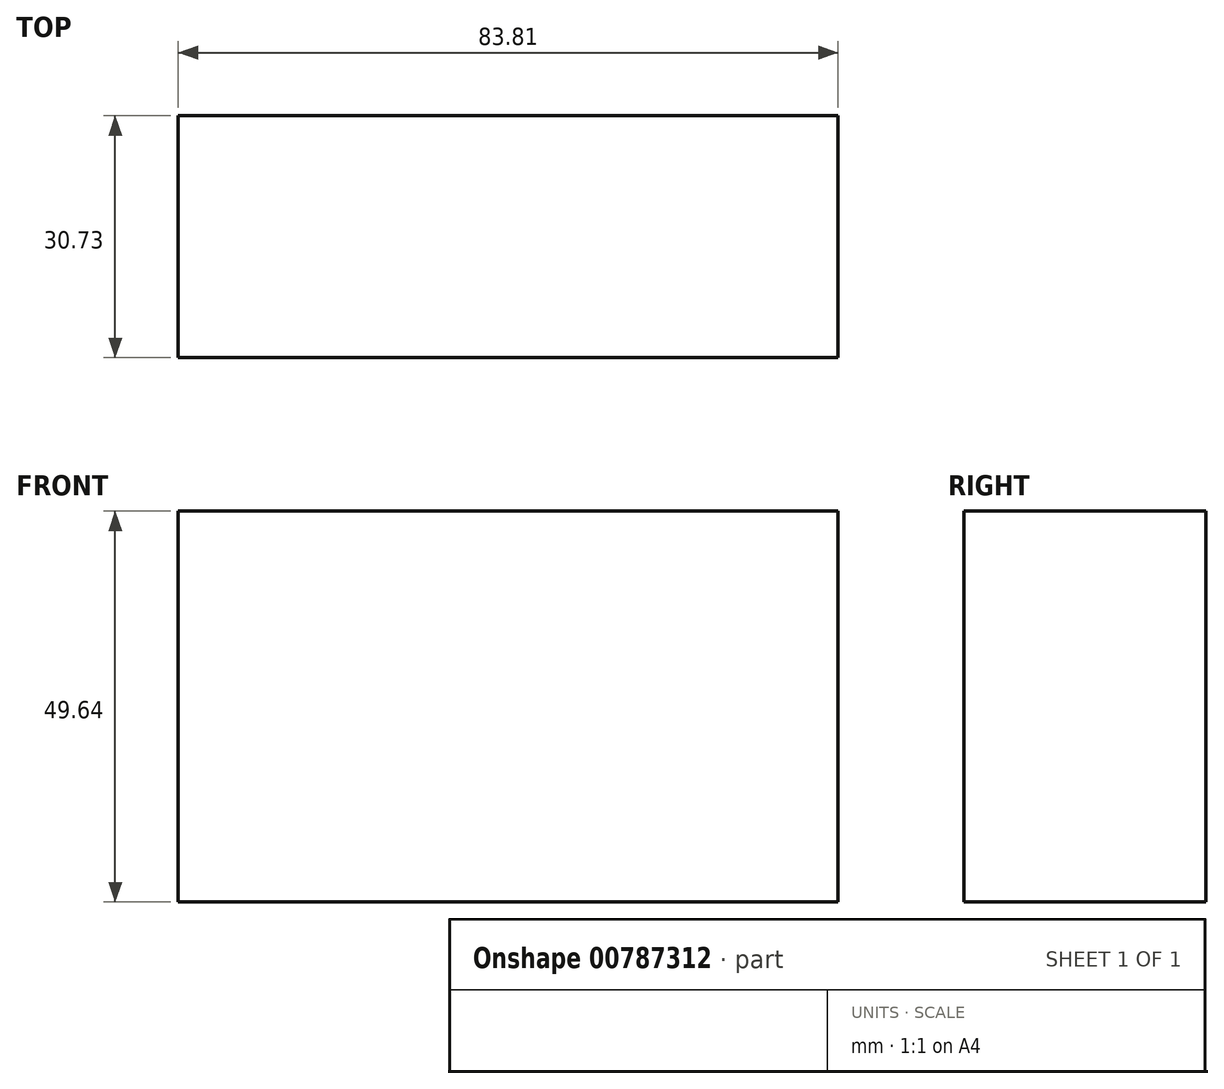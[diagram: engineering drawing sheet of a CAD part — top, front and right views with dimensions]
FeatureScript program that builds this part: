
annotation { "Feature Type Name" : "Feature", "Feature Type Description" : "" }
export const myFeature = defineFeature(function(context is Context, id is Id, definition is map)
    precondition{}
    {
        {
            var Q0;
            Q0=qCreatedBy(makeId("Front.planeOp"),FACE);
            var sketch = newSketch(context, id + "F0", { "sketchPlane" : qUnion([Q0])});
            skLineSegment(sketch, "E0.bottom", {"start": v(-38.1, 34.9) * mm, "end": v(45.7, 34.9) * mm});
            skLineSegment(sketch, "E0.top", {"start": v(-38.1, -14.75) * mm, "end": v(45.7, -14.75) * mm});
            skLineSegment(sketch, "E0.left", {"start": v(-38.1, 34.9) * mm, "end": v(-38.1, -14.75) * mm});
            skLineSegment(sketch, "E0.right", {"start": v(45.7, 34.9) * mm, "end": v(45.7, -14.75) * mm});
            skSolve(sketch);
        }
        {
            var Q0;
            Q0 = qSketchRegion(id + "F0", true);
            extrude(context, id + "F1", {"entities" : qUnion([Q0]), "depth" : 30.73 * mm, "offsetDistance" : 25.4 * mm});
        }
        {
            var Q0;
            Q0=qCreatedBy(makeId("Front.planeOp"),FACE);
            var sketch = newSketch(context, id + "F2", { "sketchPlane" : qUnion([Q0])});
            skCircle(sketch, "E1", {"center": v(4.37, 9.04) * mm, "radius": 18.75 * mm});
            skSolve(sketch);
        }
        {
            var Q0;
            Q0=qCreatedBy(makeId("Front.planeOp"),FACE);
            var sketch = newSketch(context, id + "F3", { "sketchPlane" : qUnion([Q0])});
            skCircle(sketch, "E2", {"center": v(4.07, 9.01) * mm, "radius": 14.56 * mm});
            skSolve(sketch);
        }
        {
            var Q0;
            Q0=sQuery(id+"F2.wireOp",EDGE,"E1");
            var Q1;
            Q1 = qConstructionFilter(qBodyType(qCreatedBy(id + "F3" ,EDGE), BodyType.WIRE), ConstructionObject.NO);
            extrude(context, id + "F4", {"bodyType" : ToolBodyType.SURFACE, "surfaceEntities" : qUnion([Q0, Q1]), "oppositeDirection" : true, "depth" : 25.4 * mm, "offsetDistance" : 25.4 * mm});
        }
    });
